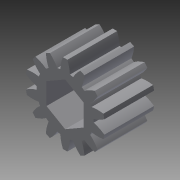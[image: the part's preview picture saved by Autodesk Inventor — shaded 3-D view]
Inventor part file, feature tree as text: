
AUTODESK INVENTOR PART (.ipt)
format: ipt  version: 2013 (Build 170138000, 138)  size: 165,376 bytes
history: native  units: in
note: dims shown in document units (in); Inventor stores cm internally (conversion verified against a paired STEP export)
features: other x2, extrude x2, sketch x2, imported_body x1
ambient origin geometry x8: Origin, YZ Plane, XZ Plane, XY Plane, X Axis, Y Axis, Z Axis, Center Point
feature tree (7):
  other  "Toughbox_d09"
  other  "Toughbox_d091"
  extrude  "Extrusion1"  Depth=0.5in TaperAngle=0.0deg
  extrude  "Extrusion2"  [1 undecoded]
  imported_body  "Base1"
  sketch  "Sketch1"  dims[d0=0.375in d1=0.5in d2=0.0in]
  sketch  "Sketch2"  dims[d3=0.5in d4=0.0in]
note: 1 required parameter value undecoded (feature->parameter linkage not recoverable at this tier; creation-order binding heuristic only, values carry confidence <= 0.55)
